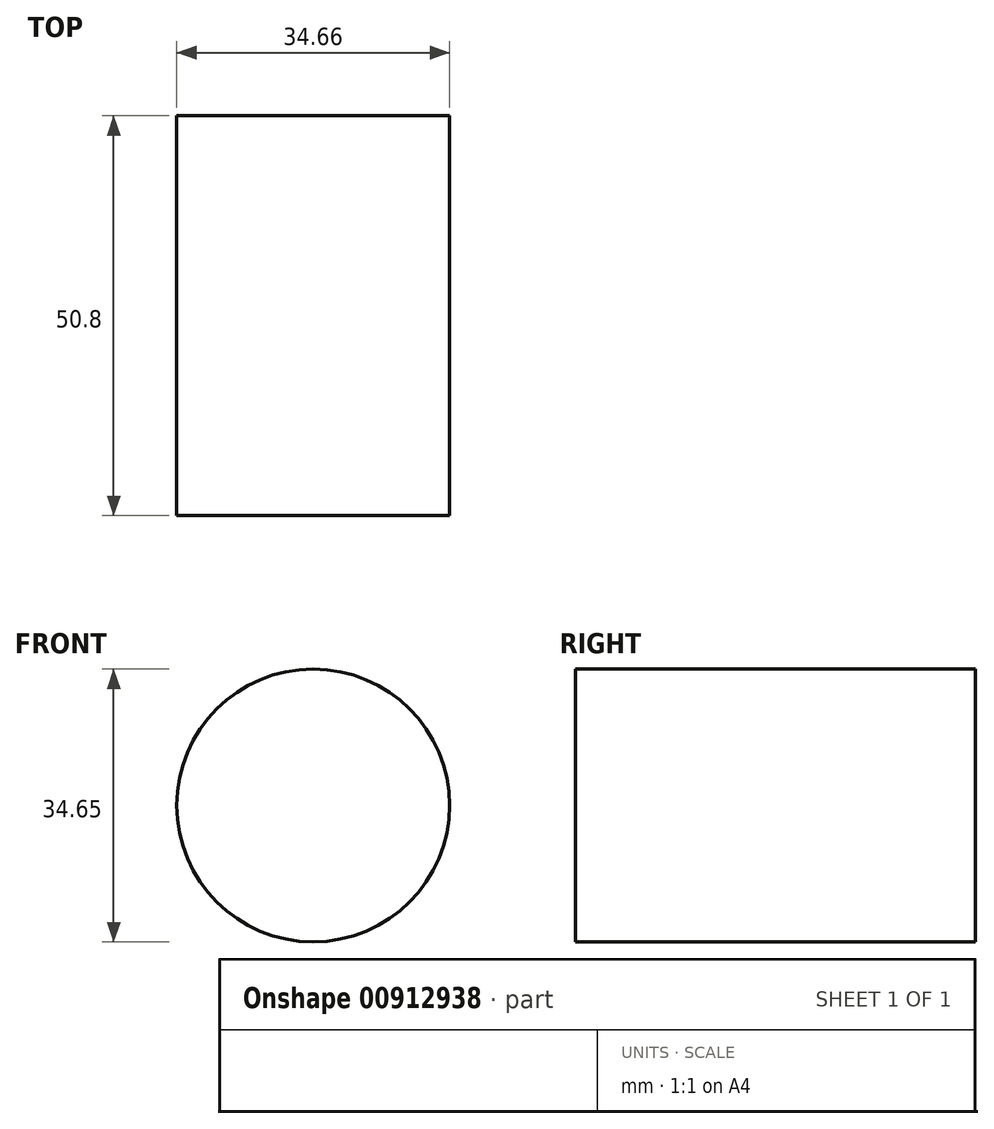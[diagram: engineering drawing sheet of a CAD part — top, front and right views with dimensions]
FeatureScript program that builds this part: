
annotation { "Feature Type Name" : "Feature", "Feature Type Description" : "" }
export const myFeature = defineFeature(function(context is Context, id is Id, definition is map)
    precondition{}
    {
        {
            var Q0;
            Q0=qCreatedBy(makeId("Front.planeOp"),FACE);
            var sketch = newSketch(context, id + "F0", { "sketchPlane" : qUnion([Q0])});
            skCircle(sketch, "E0", {"center": v(-1.02, 25.14) * mm, "radius": 17.33 * mm});
            skPoint(sketch, "E0.first.point", {"position": v(-18.35, 25.52) * mm});
            skPoint(sketch, "E0.second.point", {"position": v(7.04, 9.8) * mm});
            skPoint(sketch, "E0.third.point", {"position": v(-11.73, 38.76) * mm});
            skSolve(sketch);
        }
        {
            var Q0;
            Q0=makeQuery(id+"F0.imprint","IMPRINT",FACE,{"disambiguationData":[TD([[makeQuery(id+"F0.imprint","IMPRINT",EDGE,{"derivedFrom":sQuery(id+"F0.wireOp",EDGE,"E0")}),1.0]])]});
            extrude(context, id + "F1", {"entities" : qUnion([Q0]), "depth" : 50.8 * mm, "offsetDistance" : 25.4 * mm});
        }
    });
